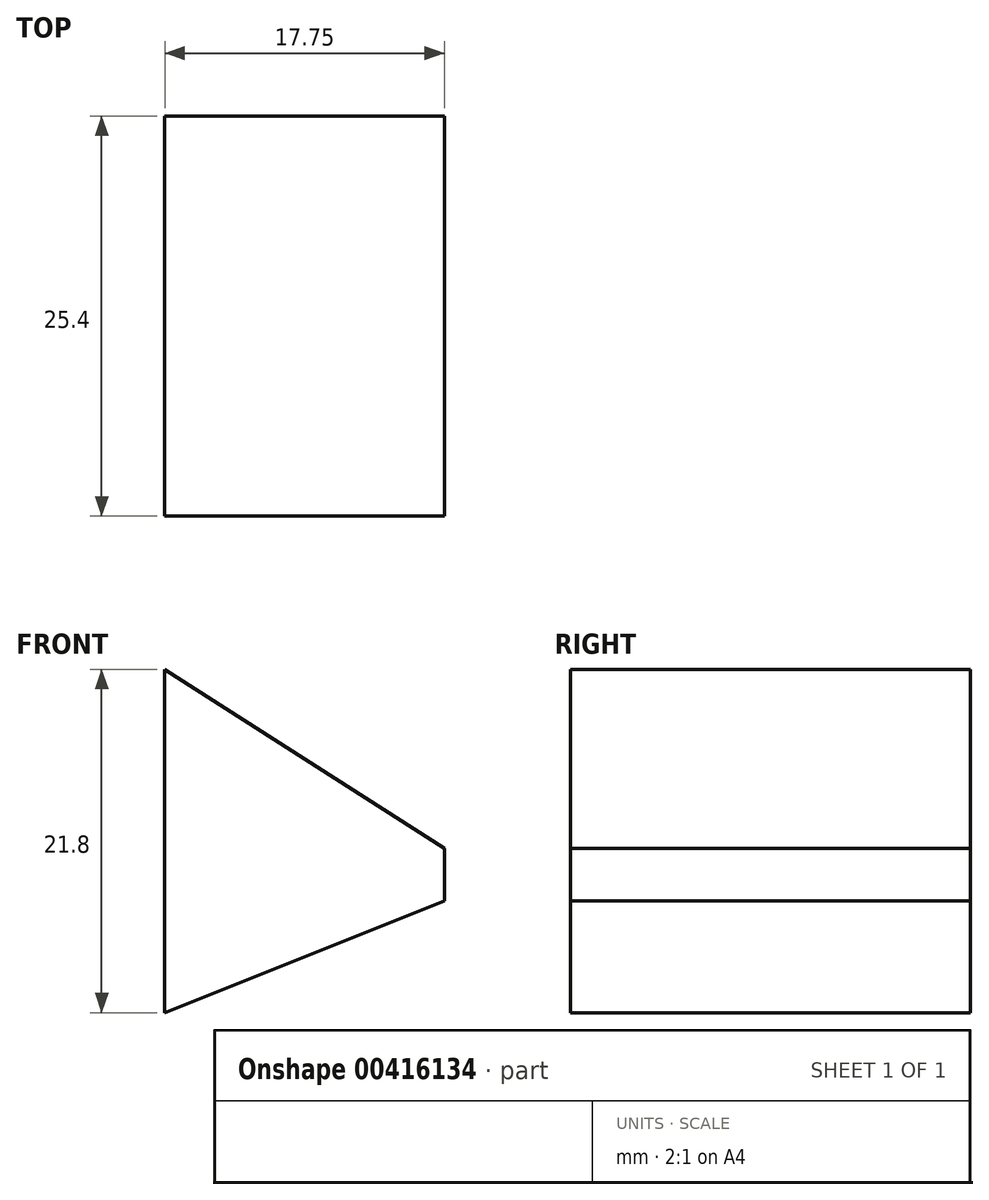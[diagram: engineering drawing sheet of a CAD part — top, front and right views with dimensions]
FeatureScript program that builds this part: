
annotation { "Feature Type Name" : "Feature", "Feature Type Description" : "" }
export const myFeature = defineFeature(function(context is Context, id is Id, definition is map)
    precondition{}
    {
        {
            var Q0;
            Q0=qCreatedBy(makeId("Front.planeOp"),FACE);
            var sketch = newSketch(context, id + "F0", { "sketchPlane" : qUnion([Q0])});
            skLineSegment(sketch, "E0", {"start": v(-93.01, 41.85) * mm, "end": v(-93.01, 20.05) * mm});
            skLineSegment(sketch, "E1", {"start": v(-75.26, 30.49) * mm, "end": v(-93.01, 41.85) * mm});
            skLineSegment(sketch, "E2", {"start": v(-93.01, 20.05) * mm, "end": v(-75.26, 27.15) * mm});
            skLineSegment(sketch, "E3", {"start": v(-75.26, 27.15) * mm, "end": v(-75.26, 30.49) * mm});
            skSolve(sketch);
        }
        {
            var Q0;
            Q0 = qSketchRegion(id + "F0", true);
            extrude(context, id + "F1", {"entities" : qUnion([Q0]), "depth" : 25.4 * mm});
        }
    });
